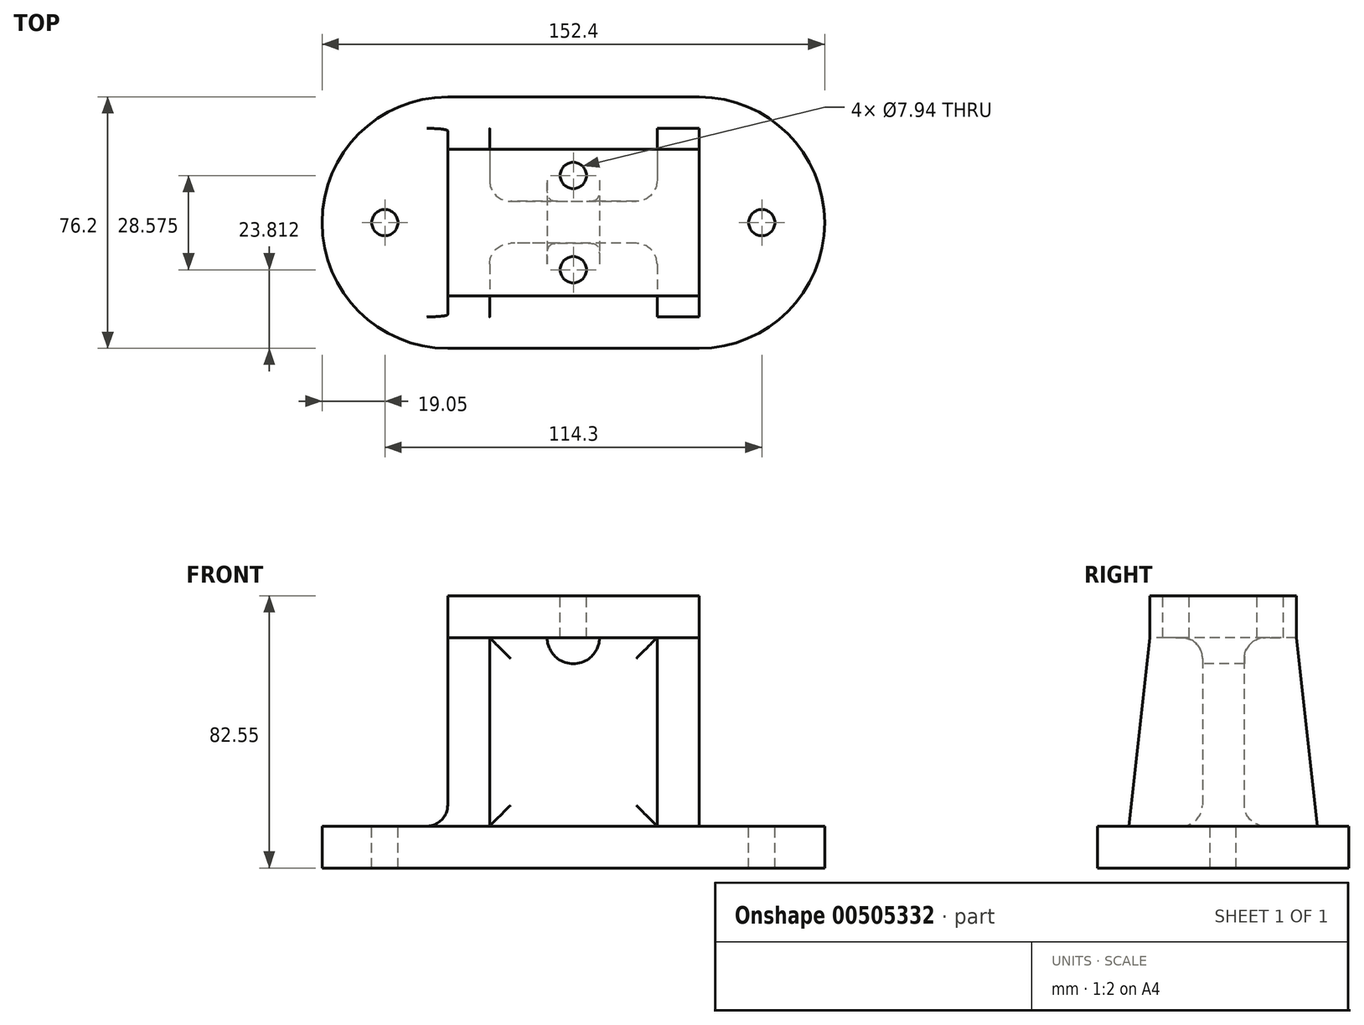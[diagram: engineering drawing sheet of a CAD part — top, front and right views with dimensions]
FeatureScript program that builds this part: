
annotation { "Feature Type Name" : "Feature", "Feature Type Description" : "" }
export const myFeature = defineFeature(function(context is Context, id is Id, definition is map)
    precondition{}
    {
        {
            var Q0;
            Q0=qCreatedBy(makeId("Top.planeOp"),FACE);
            var sketch = newSketch(context, id + "F0", { "sketchPlane" : qUnion([Q0])});
            skLineSegment(sketch, "E0.bottom", {"start": v(38.1, -38.1) * mm, "end": v(-38.1, -38.1) * mm});
            skLineSegment(sketch, "E0.top", {"start": v(38.1, 38.1) * mm, "end": v(-38.1, 38.1) * mm});
            skPoint(sketch, "E0.middle", {"position": v(0, 0) * mm});
            skPoint(sketch, "E1", {"position": v(-38.1, 0) * mm});
            skPoint(sketch, "E2", {"position": v(38.1, 0) * mm});
            skPoint(sketch, "E3", {"position": v(-38.1, 19.05) * mm});
            skPoint(sketch, "E4", {"position": v(-38.1, -19.05) * mm});
            skPoint(sketch, "E5", {"position": v(38.1, 19.05) * mm});
            skPoint(sketch, "E6", {"position": v(38.1, -19.05) * mm});
            skArc(sketch, "E7", {"start": v(-38.1, 38.1) * mm, "mid": v(-76.2, 0) * mm, "end": v(-38.1, -38.1) * mm});
            skArc(sketch, "E8", {"start": v(38.1, -38.1) * mm, "mid": v(76.2, 0) * mm, "end": v(38.1, 38.1) * mm});
            skSolve(sketch);
        }
        {
            var Q0;
            Q0 = qSketchRegion(id + "F0", true);
            extrude(context, id + "F1", {"entities" : qUnion([Q0]), "depth" : 12.7 * mm});
        }
        {
            var Q0;
            Q0=qCreatedBy(makeId("Right.planeOp"),FACE);
            var sketch = newSketch(context, id + "F2", { "sketchPlane" : qUnion([Q0])});
            skLineSegment(sketch, "E9", {"start": v(0, 82.55) * mm, "end": v(-6.26, 82.55) * mm});
            skLineSegment(sketch, "E10", {"start": v(-6.26, 69.85) * mm, "end": v(-6.26, 0) * mm});
            skLineSegment(sketch, "E11", {"start": v(-6.26, 0) * mm, "end": v(6.44, 0) * mm});
            skLineSegment(sketch, "E12", {"start": v(6.44, 0) * mm, "end": v(6.44, 69.85) * mm});
            skLineSegment(sketch, "E13", {"start": v(6.44, 82.55) * mm, "end": v(0, 82.55) * mm});
            skLineSegment(sketch, "E14", {"start": v(22.22, 69.85) * mm, "end": v(6.44, 69.85) * mm});
            skPoint(sketch, "E15", {"position": v(0, 69.85) * mm});
            skPoint(sketch, "E16", {"position": v(-128.8, 74.57) * mm});
            skPoint(sketch, "E17", {"position": v(-104.81, 115.84) * mm});
            skLineSegment(sketch, "E18", {"start": v(-6.26, 82.55) * mm, "end": v(-22.23, 82.55) * mm});
            skLineSegment(sketch, "E19", {"start": v(-22.23, 69.85) * mm, "end": v(-22.23, 82.55) * mm});
            skLineSegment(sketch, "E20", {"start": v(-22.23, 82.55) * mm, "end": v(22.22, 82.55) * mm});
            skLineSegment(sketch, "E21", {"start": v(22.22, 69.85) * mm, "end": v(22.22, 82.55) * mm});
            skLineSegment(sketch, "E22.trimOffspring", {"start": v(-6.26, 69.85) * mm, "end": v(-22.23, 69.85) * mm});
            skSolve(sketch);
        }
        {
            var Q0;
            Q0 = qSketchRegion(id + "F2", true);
            extrude(context, id + "F3", {"entities" : qUnion([Q0]), "operationType" : NewBodyOperationType.ADD, "endBound" : BoundingType.SYMMETRIC, "depth" : 76.2 * mm});
        }
        {
            var Q0;
            Q0=makeQuery(id+"F3.opExtrude","SWEPT_FACE",FACE,{"disambiguationData":[OSD([sQuery(id+"F2.wireOp",EDGE,"E10")])]});
            var sketch = newSketch(context, id + "F4", { "sketchPlane" : qUnion([Q0])});
            skArc(sketch, "E23", {"start": v(-7.94, 69.85) * mm, "mid": v(0, 61.91) * mm, "end": v(7.94, 69.85) * mm});
            skPoint(sketch, "E24", {"position": v(-7.94, 69.85) * mm});
            skPoint(sketch, "E25", {"position": v(7.94, 69.85) * mm});
            skLineSegment(sketch, "E26", {"start": v(-7.94, 69.85) * mm, "end": v(7.94, 69.85) * mm});
            skSolve(sketch);
        }
        {
            var Q0;
            Q0=makeQuery(id+"F4.imprint","IMPRINT",FACE,{"disambiguationData":[TD([[makeQuery(id+"F4.imprint","IMPRINT",EDGE,{"derivedFrom":sQuery(id+"F4.wireOp",EDGE,"E23")}),1.0]])]});
            extrude(context, id + "F5", {"entities" : qUnion([Q0]), "operationType" : NewBodyOperationType.REMOVE, "oppositeDirection" : true, "depth" : 25.4 * mm});
        }
        {
            var Q0;
            Q0=makeQuery(id+"F3.opExtrude","CAP_FACE",FACE,{"disambiguationData":[OSD([sQuery(id+"F2.wireOp",EDGE,"E10"),sQuery(id+"F2.wireOp",EDGE,"E11"),sQuery(id+"F2.wireOp",EDGE,"E12"),sQuery(id+"F2.wireOp",EDGE,"E14"),sQuery(id+"F2.wireOp",EDGE,"E19"),sQuery(id+"F2.wireOp",EDGE,"E20"),sQuery(id+"F2.wireOp",EDGE,"E21"),sQuery(id+"F2.wireOp",EDGE,"E22.trimOffspring")])],"isStart":false});
            var sketch = newSketch(context, id + "F6", { "sketchPlane" : qUnion([Q0])});
            skLineSegment(sketch, "E27", {"start": v(28.58, 12.7) * mm, "end": v(-28.58, 12.7) * mm});
            skPoint(sketch, "E28", {"position": v(0, 0) * mm});
            skLineSegment(sketch, "E29", {"start": v(-28.58, 12.7) * mm, "end": v(-22.23, 69.85) * mm});
            skLineSegment(sketch, "E30", {"start": v(-22.23, 69.85) * mm, "end": v(22.22, 69.85) * mm});
            skLineSegment(sketch, "E31", {"start": v(22.22, 69.85) * mm, "end": v(28.57, 12.7) * mm});
            skPoint(sketch, "E32.orphan", {"position": v(28.57, 0) * mm});
            skPoint(sketch, "E33.start.orphan", {"position": v(-28.58, 0) * mm});
            skSolve(sketch);
        }
        {
            var Q0;
            Q0 = qSketchRegion(id + "F6", true);
            extrude(context, id + "F7", {"entities" : qUnion([Q0]), "operationType" : NewBodyOperationType.ADD, "oppositeDirection" : true, "depth" : 12.7 * mm});
        }
        {
            var Q0;
            Q0=makeQuery(id+"F3.opExtrude","CAP_FACE",FACE,{"disambiguationData":[OSD([sQuery(id+"F2.wireOp",EDGE,"E10"),sQuery(id+"F2.wireOp",EDGE,"E11"),sQuery(id+"F2.wireOp",EDGE,"E12"),sQuery(id+"F2.wireOp",EDGE,"E14"),sQuery(id+"F2.wireOp",EDGE,"E19"),sQuery(id+"F2.wireOp",EDGE,"E20"),sQuery(id+"F2.wireOp",EDGE,"E21"),sQuery(id+"F2.wireOp",EDGE,"E22.trimOffspring")])],"isStart":true});
            var sketch = newSketch(context, id + "F8", { "sketchPlane" : qUnion([Q0])});
            skLineSegment(sketch, "E34", {"start": v(-28.58, 12.65) * mm, "end": v(28.57, 12.65) * mm});
            skLineSegment(sketch, "E35", {"start": v(-28.58, 12.65) * mm, "end": v(-22.22, 69.85) * mm});
            skLineSegment(sketch, "E36", {"start": v(-22.22, 69.85) * mm, "end": v(22.23, 69.85) * mm});
            skLineSegment(sketch, "E37", {"start": v(22.23, 69.85) * mm, "end": v(28.57, 12.65) * mm});
            skPoint(sketch, "E38.start.orphan", {"position": v(28.57, 0) * mm});
            skPoint(sketch, "E39.end.orphan", {"position": v(-28.58, 0) * mm});
            skPoint(sketch, "E39.start.orphan", {"position": v(0, 0) * mm});
            skSolve(sketch);
        }
        {
            var Q0;
            Q0 = qSketchRegion(id + "F8", true);
            extrude(context, id + "F9", {"entities" : qUnion([Q0]), "operationType" : NewBodyOperationType.ADD, "oppositeDirection" : true, "depth" : 12.7 * mm});
        }
        {
            var Q0;
            Q0=makeQuery(id+"F3.opExtrude","SWEPT_FACE",FACE,{"disambiguationData":[OSD([sQuery(id+"F2.wireOp",EDGE,"E20")])]});
            var sketch = newSketch(context, id + "F10", { "sketchPlane" : qUnion([Q0])});
            skPoint(sketch, "E40", {"position": v(0, 14.29) * mm});
            skPoint(sketch, "E41", {"position": v(0, -14.29) * mm});
            skCircle(sketch, "E42", {"center": v(0, 14.29) * mm, "radius": 3.97 * mm});
            skCircle(sketch, "E43", {"center": v(0, -14.29) * mm, "radius": 3.97 * mm});
            skPoint(sketch, "E44", {"position": v(-57.15, 0) * mm});
            skPoint(sketch, "E45", {"position": v(57.15, 0) * mm});
            skCircle(sketch, "E46", {"center": v(-57.15, 0) * mm, "radius": 3.97 * mm});
            skCircle(sketch, "E47", {"center": v(57.15, 0) * mm, "radius": 3.97 * mm});
            skSolve(sketch);
        }
        {
            var Q0;
            Q0=makeQuery(id+"F10.imprint","IMPRINT",FACE,{"disambiguationData":[TD([[makeQuery(id+"F10.imprint","IMPRINT",EDGE,{"derivedFrom":sQuery(id+"F10.wireOp",EDGE,"E42")}),1.0]])]});
            var Q1;
            Q1=makeQuery(id+"F10.imprint","IMPRINT",FACE,{"disambiguationData":[TD([[makeQuery(id+"F10.imprint","IMPRINT",EDGE,{"derivedFrom":sQuery(id+"F10.wireOp",EDGE,"E43")}),1.0]])]});
            extrude(context, id + "F11", {"entities" : qUnion([Q0, Q1]), "operationType" : NewBodyOperationType.REMOVE, "oppositeDirection" : true, "depth" : 25.4 * mm});
        }
        {
            var Q0;
            Q0=makeQuery(id+"F10.imprint","IMPRINT",FACE,{"disambiguationData":[TD([[makeQuery(id+"F10.imprint","IMPRINT",EDGE,{"derivedFrom":sQuery(id+"F10.wireOp",EDGE,"E46")}),1.0]])]});
            var Q1;
            Q1=makeQuery(id+"F10.imprint","IMPRINT",FACE,{"disambiguationData":[TD([[makeQuery(id+"F10.imprint","IMPRINT",EDGE,{"derivedFrom":sQuery(id+"F10.wireOp",EDGE,"E46")}),1.0]])]});
            var Q2;
            Q2=makeQuery(id+"F10.imprint","IMPRINT",FACE,{"disambiguationData":[TD([[makeQuery(id+"F10.imprint","IMPRINT",EDGE,{"derivedFrom":sQuery(id+"F10.wireOp",EDGE,"E47")}),1.0]])]});
            extrude(context, id + "F12", {"entities" : qUnion([Q0, Q1, Q2]), "operationType" : NewBodyOperationType.REMOVE, "endBound" : BoundingType.THROUGH_ALL, "oppositeDirection" : true, "depth" : 25.4 * mm});
        }
        {
            var Q0;
            Q0=makeQuery(id+"F7.opExtrude","SWEPT_EDGE",EDGE,{"disambiguationData":[OSD([sQuery(id+"F6.wireOp",EDGE,"E27"),sQuery(id+"F6.wireOp",EDGE,"E29")])]});
            var Q1;
            Q1=makeQuery(id+"F7.opExtrude","SWEPT_EDGE",EDGE,{"disambiguationData":[OSD([sQuery(id+"F6.wireOp",EDGE,"E27"),sQuery(id+"F6.wireOp",EDGE,"E31")])]});
            var Q2;
            Q2=makeQuery(id+"F9.boolean.opBoolean","INTERSECT",EDGE,{"derivedFrom":[makeQuery(id+"F1.opExtrude","CAP_FACE",FACE,{"disambiguationData":[OSD([sQuery(id+"F0.wireOp",EDGE,"E0.bottom"),sQuery(id+"F0.wireOp",EDGE,"E0.top"),sQuery(id+"F0.wireOp",EDGE,"E7"),sQuery(id+"F0.wireOp",EDGE,"E8")])],"isStart":false}),makeQuery(id+"F9.opExtrude","SWEPT_FACE",FACE,{"disambiguationData":[OSD([sQuery(id+"F8.wireOp",EDGE,"E37")])]})]});
            var Q3;
            Q3=makeQuery(id+"F9.boolean.opBoolean","INTERSECT",EDGE,{"derivedFrom":[makeQuery(id+"F1.opExtrude","CAP_FACE",FACE,{"disambiguationData":[OSD([sQuery(id+"F0.wireOp",EDGE,"E0.bottom"),sQuery(id+"F0.wireOp",EDGE,"E0.top"),sQuery(id+"F0.wireOp",EDGE,"E7"),sQuery(id+"F0.wireOp",EDGE,"E8")])],"isStart":false}),makeQuery(id+"F9.opExtrude","SWEPT_FACE",FACE,{"disambiguationData":[OSD([sQuery(id+"F8.wireOp",EDGE,"E35")])]})]});
            fillet(context, id + "F13", {"entities" : qUnion([Q0, Q1, Q2, Q3]), "radius" : 3 / 203.2 * mm, "tangentPropagation" : true, "allowEdgeOverflow" : false});
        }
        {
            var Q0;
            Q0=makeQuery(id+"F3.boolean.opBoolean","INTERSECT",EDGE,{"derivedFrom":[makeQuery(id+"F1.opExtrude","CAP_FACE",FACE,{"disambiguationData":[OSD([sQuery(id+"F0.wireOp",EDGE,"E0.bottom"),sQuery(id+"F0.wireOp",EDGE,"E0.top"),sQuery(id+"F0.wireOp",EDGE,"E7"),sQuery(id+"F0.wireOp",EDGE,"E8")])],"isStart":false}),makeQuery(id+"F3.opExtrude","SWEPT_FACE",FACE,{"disambiguationData":[OSD([sQuery(id+"F2.wireOp",EDGE,"E12")])]})]});
            var Q1;
            Q1=makeQuery(id+"F3.boolean.opBoolean","INTERSECT",EDGE,{"derivedFrom":[makeQuery(id+"F1.opExtrude","CAP_FACE",FACE,{"disambiguationData":[OSD([sQuery(id+"F0.wireOp",EDGE,"E0.bottom"),sQuery(id+"F0.wireOp",EDGE,"E0.top"),sQuery(id+"F0.wireOp",EDGE,"E7"),sQuery(id+"F0.wireOp",EDGE,"E8")])],"isStart":false}),makeQuery(id+"F3.opExtrude","SWEPT_FACE",FACE,{"disambiguationData":[OSD([sQuery(id+"F2.wireOp",EDGE,"E10")])]})]});
            var Q2;
            {var subQ0=sQuery(id+"F2.wireOp",EDGE,"E22.trimOffspring");var subQ1=sQuery(id+"F2.wireOp",EDGE,"E14");var subQ2=sQuery(id+"F2.wireOp",EDGE,"E10");Q2=makeQuery(id+"F5.boolean.opBoolean","SPLIT",EDGE,{"disambiguationData":[TD([makeQuery(id+"F3.opExtrude","CAP_FACE",FACE,{"disambiguationData":[OSD([subQ2,sQuery(id+"F2.wireOp",EDGE,"E11"),sQuery(id+"F2.wireOp",EDGE,"E12"),subQ1,sQuery(id+"F2.wireOp",EDGE,"E19"),sQuery(id+"F2.wireOp",EDGE,"E20"),sQuery(id+"F2.wireOp",EDGE,"E21"),subQ0])],"isStart":true})])],"derivedFrom":makeQuery(id+"F3.opExtrude","SWEPT_EDGE",EDGE,{"disambiguationData":[OSD([subQ2,subQ0])]})});}
            var Q3;
            {var subQ0=sQuery(id+"F2.wireOp",EDGE,"E22.trimOffspring");var subQ1=sQuery(id+"F2.wireOp",EDGE,"E14");var subQ2=sQuery(id+"F2.wireOp",EDGE,"E10");Q3=makeQuery(id+"F5.boolean.opBoolean","SPLIT",EDGE,{"disambiguationData":[TD([makeQuery(id+"F3.opExtrude","CAP_FACE",FACE,{"disambiguationData":[OSD([subQ2,sQuery(id+"F2.wireOp",EDGE,"E11"),sQuery(id+"F2.wireOp",EDGE,"E12"),subQ1,sQuery(id+"F2.wireOp",EDGE,"E19"),sQuery(id+"F2.wireOp",EDGE,"E20"),sQuery(id+"F2.wireOp",EDGE,"E21"),subQ0])],"isStart":false})])],"derivedFrom":makeQuery(id+"F3.opExtrude","SWEPT_EDGE",EDGE,{"disambiguationData":[OSD([subQ2,subQ0])]})});}
            var Q4;
            {var subQ0=sQuery(id+"F2.wireOp",EDGE,"E14");var subQ1=sQuery(id+"F2.wireOp",EDGE,"E22.trimOffspring");var subQ2=sQuery(id+"F2.wireOp",EDGE,"E12");Q4=makeQuery(id+"F5.boolean.opBoolean","SPLIT",EDGE,{"disambiguationData":[TD([makeQuery(id+"F3.opExtrude","CAP_FACE",FACE,{"disambiguationData":[OSD([sQuery(id+"F2.wireOp",EDGE,"E10"),sQuery(id+"F2.wireOp",EDGE,"E11"),subQ2,subQ0,sQuery(id+"F2.wireOp",EDGE,"E19"),sQuery(id+"F2.wireOp",EDGE,"E20"),sQuery(id+"F2.wireOp",EDGE,"E21"),subQ1])],"isStart":true})])],"derivedFrom":makeQuery(id+"F3.opExtrude","SWEPT_EDGE",EDGE,{"disambiguationData":[OSD([subQ2,subQ0])]})});}
            var Q5;
            {var subQ0=sQuery(id+"F2.wireOp",EDGE,"E14");var subQ1=sQuery(id+"F2.wireOp",EDGE,"E22.trimOffspring");var subQ2=sQuery(id+"F2.wireOp",EDGE,"E12");Q5=makeQuery(id+"F5.boolean.opBoolean","SPLIT",EDGE,{"disambiguationData":[TD([makeQuery(id+"F3.opExtrude","CAP_FACE",FACE,{"disambiguationData":[OSD([sQuery(id+"F2.wireOp",EDGE,"E10"),sQuery(id+"F2.wireOp",EDGE,"E11"),subQ2,subQ0,sQuery(id+"F2.wireOp",EDGE,"E19"),sQuery(id+"F2.wireOp",EDGE,"E20"),sQuery(id+"F2.wireOp",EDGE,"E21"),subQ1])],"isStart":false})])],"derivedFrom":makeQuery(id+"F3.opExtrude","SWEPT_EDGE",EDGE,{"disambiguationData":[OSD([subQ2,subQ0])]})});}
            var Q6;
            Q6=makeQuery(id+"F7.boolean.opBoolean","MERGE",EDGE,{"derivedFrom":[makeQuery(id+"F3.boolean.opBoolean","INTERSECT",EDGE,{"derivedFrom":[makeQuery(id+"F1.opExtrude","CAP_FACE",FACE,{"disambiguationData":[OSD([sQuery(id+"F0.wireOp",EDGE,"E0.bottom"),sQuery(id+"F0.wireOp",EDGE,"E0.top"),sQuery(id+"F0.wireOp",EDGE,"E7"),sQuery(id+"F0.wireOp",EDGE,"E8")])],"isStart":false}),makeQuery(id+"F3.opExtrude","CAP_FACE",FACE,{"disambiguationData":[OSD([sQuery(id+"F2.wireOp",EDGE,"E10"),sQuery(id+"F2.wireOp",EDGE,"E11"),sQuery(id+"F2.wireOp",EDGE,"E12"),sQuery(id+"F2.wireOp",EDGE,"E14"),sQuery(id+"F2.wireOp",EDGE,"E19"),sQuery(id+"F2.wireOp",EDGE,"E20"),sQuery(id+"F2.wireOp",EDGE,"E21"),sQuery(id+"F2.wireOp",EDGE,"E22.trimOffspring")])],"isStart":false})]}),makeQuery(id+"F7.opExtrude","CAP_EDGE",EDGE,{"disambiguationData":[OSD([sQuery(id+"F6.wireOp",EDGE,"E27")])],"isStart":true})]});
            var Q7;
            Q7=makeQuery(id+"F9.boolean.opBoolean","INTERSECT",EDGE,{"derivedFrom":[makeQuery(id+"F1.opExtrude","CAP_FACE",FACE,{"disambiguationData":[OSD([sQuery(id+"F0.wireOp",EDGE,"E0.bottom"),sQuery(id+"F0.wireOp",EDGE,"E0.top"),sQuery(id+"F0.wireOp",EDGE,"E7"),sQuery(id+"F0.wireOp",EDGE,"E8")])],"isStart":false}),makeQuery(id+"F9.opExtrude","CAP_FACE",FACE,{"disambiguationData":[OSD([sQuery(id+"F8.wireOp",EDGE,"E34"),sQuery(id+"F8.wireOp",EDGE,"E35"),sQuery(id+"F8.wireOp",EDGE,"E36"),sQuery(id+"F8.wireOp",EDGE,"E37")])],"isStart":true})]});
            var Q8;
            Q8=makeQuery(id+"F9.boolean.opBoolean","INTERSECT",EDGE,{"derivedFrom":[makeQuery(id+"F3.opExtrude","SWEPT_FACE",FACE,{"disambiguationData":[OSD([sQuery(id+"F2.wireOp",EDGE,"E12")])]}),makeQuery(id+"F9.opExtrude","CAP_FACE",FACE,{"disambiguationData":[OSD([sQuery(id+"F8.wireOp",EDGE,"E34"),sQuery(id+"F8.wireOp",EDGE,"E35"),sQuery(id+"F8.wireOp",EDGE,"E36"),sQuery(id+"F8.wireOp",EDGE,"E37")])],"isStart":false})]});
            var Q9;
            Q9=makeQuery(id+"F7.boolean.opBoolean","INTERSECT",EDGE,{"derivedFrom":[makeQuery(id+"F3.opExtrude","SWEPT_FACE",FACE,{"disambiguationData":[OSD([sQuery(id+"F2.wireOp",EDGE,"E12")])]}),makeQuery(id+"F7.opExtrude","CAP_FACE",FACE,{"disambiguationData":[OSD([sQuery(id+"F6.wireOp",EDGE,"E27"),sQuery(id+"F6.wireOp",EDGE,"E29"),sQuery(id+"F6.wireOp",EDGE,"E30"),sQuery(id+"F6.wireOp",EDGE,"E31")])],"isStart":false})]});
            var Q10;
            Q10=makeQuery(id+"F9.boolean.opBoolean","INTERSECT",EDGE,{"derivedFrom":[makeQuery(id+"F3.opExtrude","SWEPT_FACE",FACE,{"disambiguationData":[OSD([sQuery(id+"F2.wireOp",EDGE,"E10")])]}),makeQuery(id+"F9.opExtrude","CAP_FACE",FACE,{"disambiguationData":[OSD([sQuery(id+"F8.wireOp",EDGE,"E34"),sQuery(id+"F8.wireOp",EDGE,"E35"),sQuery(id+"F8.wireOp",EDGE,"E36"),sQuery(id+"F8.wireOp",EDGE,"E37")])],"isStart":false})]});
            var Q11;
            Q11=makeQuery(id+"F7.boolean.opBoolean","INTERSECT",EDGE,{"derivedFrom":[makeQuery(id+"F3.opExtrude","SWEPT_FACE",FACE,{"disambiguationData":[OSD([sQuery(id+"F2.wireOp",EDGE,"E10")])]}),makeQuery(id+"F7.opExtrude","CAP_FACE",FACE,{"disambiguationData":[OSD([sQuery(id+"F6.wireOp",EDGE,"E27"),sQuery(id+"F6.wireOp",EDGE,"E29"),sQuery(id+"F6.wireOp",EDGE,"E30"),sQuery(id+"F6.wireOp",EDGE,"E31")])],"isStart":false})]});
            fillet(context, id + "F14", {"entities" : qUnion([Q0, Q1, Q2, Q3, Q4, Q5, Q6, Q7, Q8, Q9, Q10, Q11]), "radius" : 6.35 * mm, "tangentPropagation" : true, "allowEdgeOverflow" : false});
        }
    });
